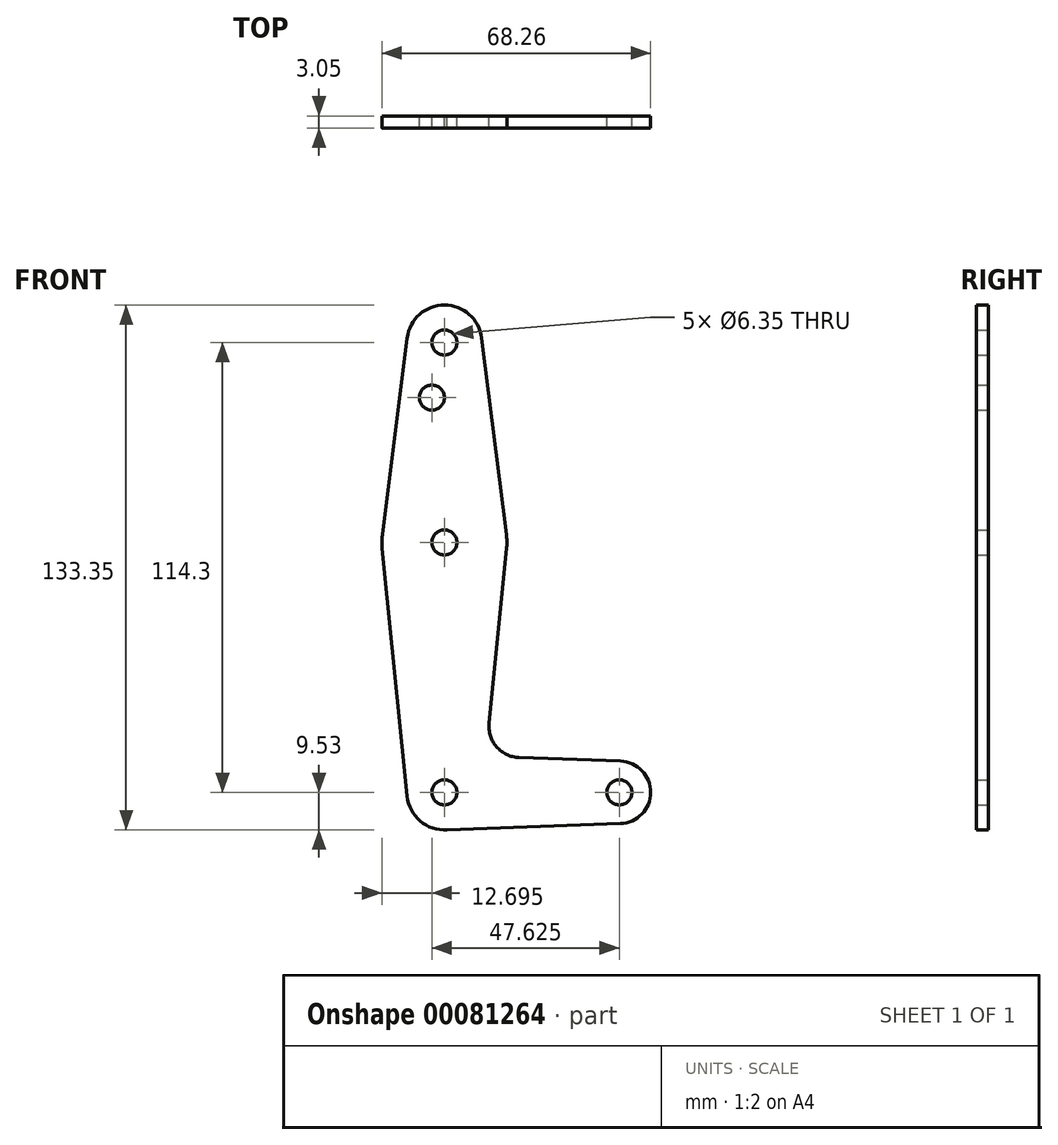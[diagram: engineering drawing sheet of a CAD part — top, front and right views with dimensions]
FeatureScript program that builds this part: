
annotation { "Feature Type Name" : "Feature", "Feature Type Description" : "" }
export const myFeature = defineFeature(function(context is Context, id is Id, definition is map)
    precondition{}
    {
        {
            var Q0;
            Q0=qCreatedBy(makeId("Front.planeOp"),FACE);
            var sketch = newSketch(context, id + "F0", { "sketchPlane" : qUnion([Q0])});
            skCircle(sketch, "E0", {"center": v(0, 50.8) * mm, "radius": 9.53 * mm});
            skCircle(sketch, "E1", {"center": v(0, 0) * mm, "radius": 15.88 * mm});
            skCircle(sketch, "E2", {"center": v(0, -63.5) * mm, "radius": 9.53 * mm});
            skCircle(sketch, "E3", {"center": v(44.45, -63.5) * mm, "radius": 7.94 * mm});
            skLineSegment(sketch, "E4", {"start": v(-9.45, 52) * mm, "end": v(-15.75, 1.98) * mm});
            skLineSegment(sketch, "E5", {"start": v(9.45, 52) * mm, "end": v(15.75, 1.98) * mm});
            skLineSegment(sketch, "E6", {"start": v(-15.8, -1.59) * mm, "end": v(-9.48, -64.45) * mm});
            skLineSegment(sketch, "E7", {"start": v(15.8, -1.59) * mm, "end": v(11.34, -45.91) * mm});
            skLineSegment(sketch, "E8", {"start": v(18.97, -54.65) * mm, "end": v(44.73, -55.57) * mm});
            skLineSegment(sketch, "E9", {"start": v(0, -73.03) * mm, "end": v(44.73, -71.43) * mm});
            skCircle(sketch, "E10", {"center": v(0, 50.8) * mm, "radius": 3.18 * mm});
            skCircle(sketch, "E11", {"center": v(-3.18, 36.8) * mm, "radius": 3.18 * mm});
            skCircle(sketch, "E12", {"center": v(0, 0) * mm, "radius": 3.18 * mm});
            skCircle(sketch, "E13", {"center": v(0, -63.5) * mm, "radius": 3.18 * mm});
            skCircle(sketch, "E14", {"center": v(44.45, -63.5) * mm, "radius": 3.18 * mm});
            skPoint(sketch, "E15.newPointB", {"position": v(0, -53.98) * mm});
            skArc(sketch, "E15.filletArc", {"start": v(11.34, -45.91) * mm, "mid": v(13.26, -51.93) * mm, "end": v(18.97, -54.65) * mm});
            skSolve(sketch);
        }
        {
            var Q0;
            Q0 = qSketchRegion(id + "F0", true);
            extrude(context, id + "F1", {"entities" : qUnion([Q0]), "depth" : 3.05 * mm});
        }
    });
